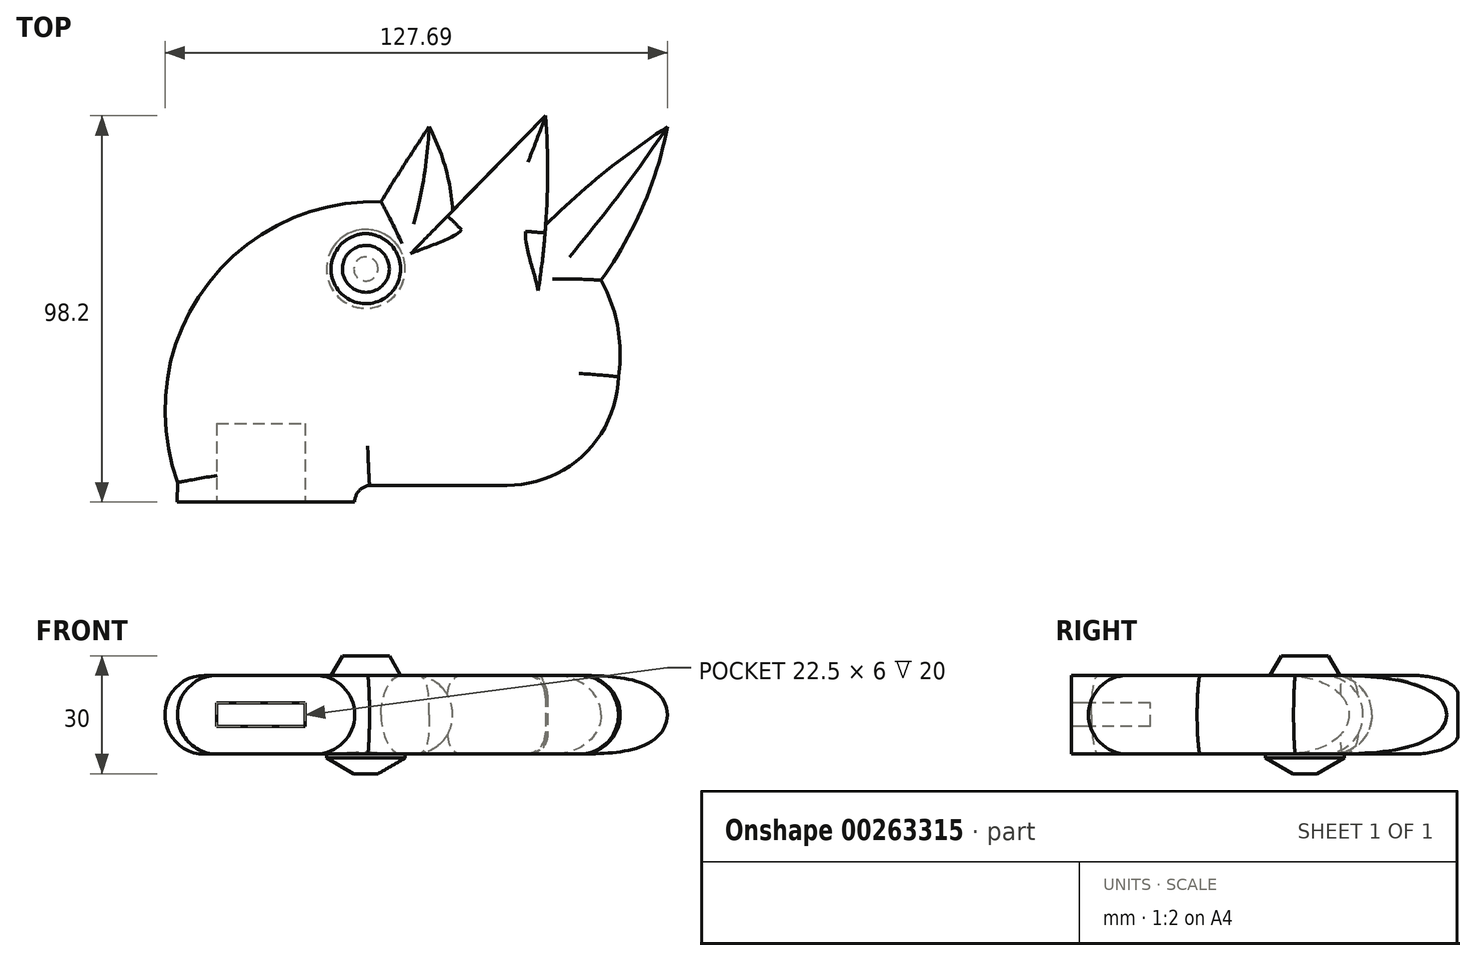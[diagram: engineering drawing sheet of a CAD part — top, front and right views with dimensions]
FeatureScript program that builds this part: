
annotation { "Feature Type Name" : "Feature", "Feature Type Description" : "" }
export const myFeature = defineFeature(function(context is Context, id is Id, definition is map)
    precondition{}
    {
        {
            var Q0;
            Q0=qCreatedBy(makeId("Top.planeOp"),FACE);
            var sketch = newSketch(context, id + "F0", { "sketchPlane" : qUnion([Q0])});
            skArc(sketch, "E0", {"start": v(-69.56, -48.3) * mm, "mid": v(-88.08, -45.25) * mm, "end": v(-106.8, -43.78) * mm});
            skArc(sketch, "E1", {"start": v(-106.8, -43.78) * mm, "mid": v(-96.39, -62.57) * mm, "end": v(-80.73, -77.27) * mm});
            skArc(sketch, "E2", {"start": v(-80.73, -77.27) * mm, "mid": v(-98.26, -84.7) * mm, "end": v(-114.23, -95.07) * mm});
            skArc(sketch, "E3", {"start": v(-114.23, -95.07) * mm, "mid": v(-98.6, -104.41) * mm, "end": v(-80.73, -107.98) * mm});
            skArc(sketch, "E4", {"start": v(-80.73, -107.98) * mm, "mid": v(-90.04, -123.58) * mm, "end": v(-94.69, -141.13) * mm});
            skArc(sketch, "E5", {"start": v(-94.69, -141.13) * mm, "mid": v(-78.8, -139.7) * mm, "end": v(-63.98, -133.8) * mm});
            skArc(sketch, "E6", {"start": v(-63.98, -133.8) * mm, "mid": v(40.14, -139.24) * mm, "end": v(30.94, -35.4) * mm});
            skArc(sketch, "E7", {"start": v(-31.41, -22.87) * mm, "mid": v(-53.17, -31.57) * mm, "end": v(-69.56, -48.3) * mm});
            skCircle(sketch, "E8", {"center": v(-12, -90) * mm, "radius": 35 * mm});
            skLineSegment(sketch, "E9", {"start": v(-12, -90) * mm, "end": v(-12, 0) * mm});
            skLineSegment(sketch, "E10", {"start": v(-12, 0) * mm, "end": v(0, 0) * mm});
            skLineSegment(sketch, "E11", {"start": v(-31.41, -22.87) * mm, "end": v(-12, 0) * mm});
            skLineSegment(sketch, "E12", {"start": v(-31.41, -22.87) * mm, "end": v(0, 0) * mm});
            skArc(sketch, "E13", {"start": v(30.94, -35.4) * mm, "mid": v(57.65, 8.29) * mm, "end": v(64.82, 58.99) * mm});
            skLineSegment(sketch, "E14", {"start": v(64.82, 42.9) * mm, "end": v(70.1, 125.75) * mm});
            skLineSegment(sketch, "E15", {"start": v(70.1, 125.75) * mm, "end": v(73.47, 146.99) * mm});
            skLineSegment(sketch, "E16", {"start": v(73.47, 146.99) * mm, "end": v(91.25, 150.97) * mm});
            skArc(sketch, "E17", {"start": v(93.55, 168.05) * mm, "mid": v(98.13, 170.3) * mm, "end": v(101.04, 174.5) * mm});
            skArc(sketch, "E18", {"start": v(101.04, 174.5) * mm, "mid": v(98.19, 178.86) * mm, "end": v(93.55, 181.22) * mm});
            skArc(sketch, "E19", {"start": v(91.25, 150.97) * mm, "mid": v(97.19, 153.5) * mm, "end": v(101.85, 157.96) * mm});
            skArc(sketch, "E20", {"start": v(101.85, 157.96) * mm, "mid": v(99.5, 164.5) * mm, "end": v(93.55, 168.05) * mm});
            skArc(sketch, "E21", {"start": v(93.55, 181.22) * mm, "mid": v(100.45, 185.24) * mm, "end": v(104.38, 192.2) * mm});
            skArc(sketch, "E22", {"start": v(16.27, 5.35) * mm, "mid": v(27.94, 20.47) * mm, "end": v(35.96, 37.8) * mm});
            skLineSegment(sketch, "E23", {"start": v(16.27, 5.35) * mm, "end": v(12.02, 0.97) * mm});
            skLineSegment(sketch, "E24", {"start": v(12.02, 54.47) * mm, "end": v(16.98, 220.58) * mm});
            skLineSegment(sketch, "E25", {"start": v(16.98, 220.58) * mm, "end": v(16.98, 230.48) * mm});
            skArc(sketch, "E26", {"start": v(20.74, 234.78) * mm, "mid": v(18.05, 233.34) * mm, "end": v(16.98, 230.48) * mm});
            skLineSegment(sketch, "E27", {"start": v(20.74, 234.78) * mm, "end": v(55.67, 234.78) * mm});
            skArc(sketch, "E28", {"start": v(55.67, 234.78) * mm, "mid": v(75.45, 242.82) * mm, "end": v(84, 262.38) * mm});
            skArc(sketch, "E29", {"start": v(84, 262.38) * mm, "mid": v(83.8, 275) * mm, "end": v(79.59, 286.9) * mm});
            skArc(sketch, "E30", {"start": v(79.59, 286.9) * mm, "mid": v(90.12, 305.47) * mm, "end": v(96.46, 325.87) * mm});
            skArc(sketch, "E31", {"start": v(96.46, 325.87) * mm, "mid": v(80.34, 314.22) * mm, "end": v(65.52, 300.95) * mm});
            skArc(sketch, "E32", {"start": v(65.52, 300.95) * mm, "mid": v(66.02, 314.82) * mm, "end": v(65.52, 328.68) * mm});
            skArc(sketch, "E33", {"start": v(41.86, 304.54) * mm, "mid": v(40.03, 315.53) * mm, "end": v(35.9, 325.87) * mm});
            skArc(sketch, "E34", {"start": v(35.9, 325.87) * mm, "mid": v(29.68, 316.4) * mm, "end": v(23.68, 306.81) * mm});
            skArc(sketch, "E35", {"start": v(23.68, 306.81) * mm, "mid": v(-21.12, 284.92) * mm, "end": v(-28, 235.53) * mm});
            skLineSegment(sketch, "E36", {"start": v(-31.41, -22.87) * mm, "end": v(-28, 235.53) * mm});
            skLineSegment(sketch, "E37", {"start": v(0, 0) * mm, "end": v(0, 302.13) * mm});
            skLineSegment(sketch, "E38", {"start": v(12.02, 0.97) * mm, "end": v(-31.41, -22.87) * mm});
            skLineSegment(sketch, "E39", {"start": v(0, 0) * mm, "end": v(12.02, 0.97) * mm});
            skLineSegment(sketch, "E40", {"start": v(12.02, 0.97) * mm, "end": v(30.94, -35.4) * mm});
            skLineSegment(sketch, "E41", {"start": v(64.82, 58.99) * mm, "end": v(46.6, 104.17) * mm});
            skLineSegment(sketch, "E42", {"start": v(12.02, 0.97) * mm, "end": v(12.02, 54.47) * mm});
            skLineSegment(sketch, "E43", {"start": v(-29.54, 119.27) * mm, "end": v(13.94, 118.7) * mm});
            skLineSegment(sketch, "E44", {"start": v(35.96, 37.8) * mm, "end": v(38.97, 138.47) * mm});
            skArc(sketch, "E45", {"start": v(104.38, 192.2) * mm, "mid": v(74.78, 206.52) * mm, "end": v(46.71, 189.39) * mm});
            skArc(sketch, "E46", {"start": v(46.71, 189.39) * mm, "mid": v(41.3, 164.16) * mm, "end": v(38.97, 138.47) * mm});
            skLineSegment(sketch, "E47", {"start": v(104.38, 192.2) * mm, "end": v(93.55, 181.22) * mm});
            skLineSegment(sketch, "E48", {"start": v(93.55, 168.05) * mm, "end": v(101.85, 157.96) * mm});
            skLineSegment(sketch, "E49", {"start": v(93.55, 181.22) * mm, "end": v(101.04, 174.5) * mm});
            skLineSegment(sketch, "E50", {"start": v(93.55, 168.05) * mm, "end": v(101.04, 174.5) * mm});
            skLineSegment(sketch, "E51", {"start": v(41.86, 304.54) * mm, "end": v(65.52, 328.68) * mm});
            skLineSegment(sketch, "E52", {"start": v(16.98, 230.48) * mm, "end": v(-28.07, 230.48) * mm});
            skLineSegment(sketch, "E53", {"start": v(12.02, 0.97) * mm, "end": v(-31.1, 0.49) * mm});
            skPoint(sketch, "E53.endSnap0", {"position": v(6.01, 0.49) * mm});
            skLineSegment(sketch, "E54", {"start": v(12.02, 0.97) * mm, "end": v(43.15, -20.17) * mm});
            skSolve(sketch);
        }
        {
            var Q0;
            {var subQ0=sQuery(id+"F0.wireOp",EDGE,"E38");var subQ1=sQuery(id+"F0.wireOp",EDGE,"E9");var subQ2=makeQuery(id+"F0.imprint","INTERSECT",VERTEX,{"derivedFrom":[subQ1,subQ0]});Q0=makeQuery(id+"F0.imprint","IMPRINT",FACE,{"disambiguationData":[TD([[makeQuery(id+"F0.imprint","IMPRINT",EDGE,{"disambiguationData":[TD([[subQ2,-1.0]])],"derivedFrom":subQ1}),1.0]])]});}
            var Q1;
            {var subQ0=sQuery(id+"F0.wireOp",EDGE,"E11");Q1=makeQuery(id+"F0.imprint","IMPRINT",FACE,{"disambiguationData":[TD([[makeQuery(id+"F0.imprint","IMPRINT",EDGE,{"derivedFrom":subQ0}),-1.0]])]});}
            var Q2;
            {var subQ0=sQuery(id+"F0.wireOp",EDGE,"E39");Q2=makeQuery(id+"F0.imprint","IMPRINT",FACE,{"disambiguationData":[TD([[makeQuery(id+"F0.imprint","IMPRINT",EDGE,{"derivedFrom":subQ0}),1.0]])]});}
            var Q3;
            Q3=makeQuery(id+"F0.imprint","IMPRINT",FACE,{"disambiguationData":[TD([[makeQuery(id+"F0.imprint","IMPRINT",EDGE,{"derivedFrom":sQuery(id+"F0.wireOp",EDGE,"E0")}),1.0]])]});
            var Q4;
            {var subQ5=sQuery(id+"F0.wireOp",EDGE,"E39");Q4=makeQuery(id+"F0.imprint","IMPRINT",FACE,{"disambiguationData":[TD([[makeQuery(id+"F0.imprint","IMPRINT",EDGE,{"derivedFrom":subQ5}),-1.0]])]});}
            var Q5;
            {var subQ2=sQuery(id+"F0.wireOp",EDGE,"E10");Q5=makeQuery(id+"F0.imprint","IMPRINT",FACE,{"disambiguationData":[TD([[makeQuery(id+"F0.imprint","IMPRINT",EDGE,{"derivedFrom":subQ2}),1.0]])]});}
            var Q6;
            {var subQ0=sQuery(id+"F0.wireOp",EDGE,"E10");Q6=makeQuery(id+"F0.imprint","IMPRINT",FACE,{"disambiguationData":[TD([[makeQuery(id+"F0.imprint","IMPRINT",EDGE,{"derivedFrom":subQ0}),-1.0]])]});}
            var Q7;
            {var subQ0=sQuery(id+"F0.wireOp",EDGE,"E40");Q7=makeQuery(id+"F0.imprint","IMPRINT",FACE,{"disambiguationData":[TD([[makeQuery(id+"F0.imprint","IMPRINT",EDGE,{"derivedFrom":subQ0}),1.0]])]});}
            extrude(context, id + "F1", {"entities" : qUnion([Q0, Q1, Q2, Q3, Q4, Q5, Q6, Q7]), "depth" : 20 * mm});
        }
        {
            var Q0;
            {var subQ1=sQuery(id+"F0.wireOp",EDGE,"E14");Q0=makeQuery(id+"F0.imprint","IMPRINT",FACE,{"disambiguationData":[TD([[makeQuery(id+"F0.imprint","IMPRINT",EDGE,{"derivedFrom":subQ1}),1.0]])]});}
            extrude(context, id + "F2", {"entities" : qUnion([Q0]), "depth" : 20 * mm});
        }
        {
            var Q0;
            {var subQ0=sQuery(id+"F0.wireOp",EDGE,"E43");var subQ1=sQuery(id+"F0.wireOp",EDGE,"E36");var subQ2=makeQuery(id+"F0.imprint","INTERSECT",VERTEX,{"derivedFrom":[subQ1,subQ0]});Q0=makeQuery(id+"F0.imprint","IMPRINT",FACE,{"disambiguationData":[TD([[makeQuery(id+"F0.imprint","IMPRINT",EDGE,{"disambiguationData":[TD([[subQ2,1.0]])],"derivedFrom":subQ1}),-1.0]])]});}
            var Q1;
            {var subQ5=sQuery(id+"F0.wireOp",EDGE,"E42");Q1=makeQuery(id+"F0.imprint","IMPRINT",FACE,{"disambiguationData":[TD([[makeQuery(id+"F0.imprint","IMPRINT",EDGE,{"derivedFrom":subQ5}),1.0]])]});}
            var Q2;
            {var subQ0=sQuery(id+"F0.wireOp",EDGE,"E43");var subQ1=sQuery(id+"F0.wireOp",EDGE,"E36");var subQ2=makeQuery(id+"F0.imprint","INTERSECT",VERTEX,{"derivedFrom":[subQ1,subQ0]});Q2=makeQuery(id+"F0.imprint","IMPRINT",FACE,{"disambiguationData":[TD([[makeQuery(id+"F0.imprint","IMPRINT",EDGE,{"disambiguationData":[TD([[subQ2,-1.0]])],"derivedFrom":subQ1}),-1.0]])]});}
            var Q3;
            {var subQ7=sQuery(id+"F0.wireOp",EDGE,"E25");Q3=makeQuery(id+"F0.imprint","IMPRINT",FACE,{"disambiguationData":[TD([[makeQuery(id+"F0.imprint","IMPRINT",EDGE,{"derivedFrom":subQ7}),1.0]])]});}
            extrude(context, id + "F3", {"entities" : qUnion([Q0, Q1, Q2, Q3]), "depth" : 20 * mm});
        }
        {
            var Q0;
            {var subQ0=sQuery(id+"F0.wireOp",EDGE,"E36");var subQ1=sQuery(id+"F0.wireOp",EDGE,"E35");var subQ2=makeQuery(id+"F0.imprint","INTERSECT",VERTEX,{"derivedFrom":[subQ1,subQ0]});Q0=makeQuery(id+"F0.imprint","IMPRINT",FACE,{"disambiguationData":[TD([[makeQuery(id+"F0.imprint","IMPRINT",EDGE,{"disambiguationData":[TD([[subQ2,1.0]])],"derivedFrom":subQ1}),1.0]])]});}
            var Q1;
            {var subQ4=sQuery(id+"F0.wireOp",EDGE,"E26");Q1=makeQuery(id+"F0.imprint","IMPRINT",FACE,{"disambiguationData":[TD([[makeQuery(id+"F0.imprint","IMPRINT",EDGE,{"derivedFrom":subQ4}),-1.0]])]});}
            extrude(context, id + "F4", {"entities" : qUnion([Q0, Q1]), "depth" : 20 * mm});
        }
        {
            var Q0;
            Q0=makeQuery(id+"F1.opExtrude","CAP_EDGE",EDGE,{"disambiguationData":[OSD([sQuery(id+"F0.wireOp",EDGE,"E36")])],"isStart":false});
            var Q1;
            Q1=makeQuery(id+"F1.opExtrude","CAP_EDGE",EDGE,{"disambiguationData":[OSD([sQuery(id+"F0.wireOp",EDGE,"E24")])],"isStart":false});
            var Q2;
            Q2=makeQuery(id+"F1.opExtrude","CAP_EDGE",EDGE,{"disambiguationData":[OSD([sQuery(id+"F0.wireOp",EDGE,"E42")])],"isStart":false});
            var Q3;
            Q3=makeQuery(id+"F1.opExtrude","CAP_EDGE",EDGE,{"disambiguationData":[OSD([sQuery(id+"F0.wireOp",EDGE,"E25")])],"isStart":false});
            var Q4;
            Q4=makeQuery(id+"F1.opExtrude","CAP_EDGE",EDGE,{"disambiguationData":[OSD([sQuery(id+"F0.wireOp",EDGE,"E35")])],"isStart":false});
            var Q5;
            Q5=makeQuery(id+"F1.opExtrude","CAP_EDGE",EDGE,{"disambiguationData":[OSD([sQuery(id+"F0.wireOp",EDGE,"E26")])],"isStart":false});
            var Q6;
            Q6=makeQuery(id+"F1.opExtrude","CAP_EDGE",EDGE,{"disambiguationData":[OSD([sQuery(id+"F0.wireOp",EDGE,"E42")])],"isStart":true});
            var Q7;
            Q7=makeQuery(id+"F1.opExtrude","CAP_EDGE",EDGE,{"disambiguationData":[OSD([sQuery(id+"F0.wireOp",EDGE,"E25")])],"isStart":true});
            var Q8;
            Q8=makeQuery(id+"F1.opExtrude","CAP_EDGE",EDGE,{"disambiguationData":[OSD([sQuery(id+"F0.wireOp",EDGE,"E36")])],"isStart":true});
            var Q9;
            Q9=makeQuery(id+"F1.opExtrude","CAP_EDGE",EDGE,{"disambiguationData":[OSD([sQuery(id+"F0.wireOp",EDGE,"E35")])],"isStart":true});
            var Q10;
            Q10=makeQuery(id+"F1.opExtrude","CAP_EDGE",EDGE,{"disambiguationData":[OSD([sQuery(id+"F0.wireOp",EDGE,"E26")])],"isStart":true});
            var Q11;
            Q11=makeQuery(id+"F1.opExtrude","CAP_EDGE",EDGE,{"disambiguationData":[OSD([sQuery(id+"F0.wireOp",EDGE,"E22")])],"isStart":false});
            var Q12;
            Q12=makeQuery(id+"F1.opExtrude","CAP_EDGE",EDGE,{"disambiguationData":[OSD([sQuery(id+"F0.wireOp",EDGE,"E23")])],"isStart":false});
            var Q13;
            Q13=makeQuery(id+"F1.opExtrude","CAP_EDGE",EDGE,{"disambiguationData":[OSD([sQuery(id+"F0.wireOp",EDGE,"E44")])],"isStart":false});
            var Q14;
            Q14=makeQuery(id+"F1.opExtrude","CAP_EDGE",EDGE,{"disambiguationData":[OSD([sQuery(id+"F0.wireOp",EDGE,"E45")])],"isStart":false});
            var Q15;
            Q15=makeQuery(id+"F1.opExtrude","CAP_EDGE",EDGE,{"disambiguationData":[OSD([sQuery(id+"F0.wireOp",EDGE,"E22")])],"isStart":true});
            var Q16;
            Q16=makeQuery(id+"F1.opExtrude","CAP_EDGE",EDGE,{"disambiguationData":[OSD([sQuery(id+"F0.wireOp",EDGE,"E44")])],"isStart":true});
            var Q17;
            Q17=makeQuery(id+"F1.opExtrude","CAP_EDGE",EDGE,{"disambiguationData":[OSD([sQuery(id+"F0.wireOp",EDGE,"E45")])],"isStart":true});
            var Q18;
            Q18=makeQuery(id+"F1.opExtrude","CAP_EDGE",EDGE,{"disambiguationData":[OSD([sQuery(id+"F0.wireOp",EDGE,"E13")])],"isStart":false});
            var Q19;
            Q19=makeQuery(id+"F1.opExtrude","CAP_EDGE",EDGE,{"disambiguationData":[OSD([sQuery(id+"F0.wireOp",EDGE,"E14")])],"isStart":false});
            var Q20;
            Q20=makeQuery(id+"F1.opExtrude","CAP_EDGE",EDGE,{"disambiguationData":[OSD([sQuery(id+"F0.wireOp",EDGE,"E15")])],"isStart":false});
            var Q21;
            Q21=makeQuery(id+"F1.opExtrude","CAP_EDGE",EDGE,{"disambiguationData":[OSD([sQuery(id+"F0.wireOp",EDGE,"E16")])],"isStart":false});
            var Q22;
            Q22=makeQuery(id+"F1.opExtrude","CAP_EDGE",EDGE,{"disambiguationData":[OSD([sQuery(id+"F0.wireOp",EDGE,"E16")])],"isStart":true});
            var Q23;
            Q23=makeQuery(id+"F1.opExtrude","CAP_EDGE",EDGE,{"disambiguationData":[OSD([sQuery(id+"F0.wireOp",EDGE,"E15")])],"isStart":true});
            var Q24;
            Q24=makeQuery(id+"F1.opExtrude","CAP_EDGE",EDGE,{"disambiguationData":[OSD([sQuery(id+"F0.wireOp",EDGE,"E14")])],"isStart":true});
            var Q25;
            Q25=makeQuery(id+"F1.opExtrude","CAP_EDGE",EDGE,{"disambiguationData":[OSD([sQuery(id+"F0.wireOp",EDGE,"E13")])],"isStart":true});
            var Q26;
            Q26=makeQuery(id+"F1.opExtrude","CAP_EDGE",EDGE,{"disambiguationData":[OSD([sQuery(id+"F0.wireOp",EDGE,"E6")])],"isStart":false});
            var Q27;
            Q27=makeQuery(id+"F1.opExtrude","CAP_EDGE",EDGE,{"disambiguationData":[OSD([sQuery(id+"F0.wireOp",EDGE,"E8")])],"isStart":false});
            var Q28;
            Q28=makeQuery(id+"F1.opExtrude","CAP_EDGE",EDGE,{"disambiguationData":[OSD([sQuery(id+"F0.wireOp",EDGE,"E7")])],"isStart":false});
            var Q29;
            Q29=makeQuery(id+"F1.opExtrude","CAP_EDGE",EDGE,{"disambiguationData":[OSD([sQuery(id+"F0.wireOp",EDGE,"E8")])],"isStart":true});
            var Q30;
            Q30=makeQuery(id+"F1.opExtrude","CAP_EDGE",EDGE,{"disambiguationData":[OSD([sQuery(id+"F0.wireOp",EDGE,"E7")])],"isStart":true});
            var Q31;
            Q31=makeQuery(id+"F1.opExtrude","CAP_EDGE",EDGE,{"disambiguationData":[OSD([sQuery(id+"F0.wireOp",EDGE,"E6")])],"isStart":true});
            fillet(context, id + "F5", {"entities" : qUnion([Q0, Q1, Q2, Q3, Q4, Q5, Q6, Q7, Q8, Q9, Q10, Q11, Q12, Q13, Q14, Q15, Q16, Q17, Q18, Q19, Q20, Q21, Q22, Q23, Q24, Q25, Q26, Q27, Q28, Q29, Q30, Q31]), "radius" : 10 * mm, "tangentPropagation" : true, "allowEdgeOverflow" : false});
        }
        {
            var Q0;
            Q0=makeQuery(id+"F1.opExtrude","CAP_EDGE",EDGE,{"disambiguationData":[OSD([sQuery(id+"F0.wireOp",EDGE,"E0")])],"isStart":false});
            var Q1;
            Q1=makeQuery(id+"F1.opExtrude","CAP_EDGE",EDGE,{"disambiguationData":[OSD([sQuery(id+"F0.wireOp",EDGE,"E1")])],"isStart":false});
            var Q2;
            Q2=makeQuery(id+"F1.opExtrude","CAP_EDGE",EDGE,{"disambiguationData":[OSD([sQuery(id+"F0.wireOp",EDGE,"E5")])],"isStart":false});
            var Q3;
            Q3=makeQuery(id+"F1.opExtrude","CAP_EDGE",EDGE,{"disambiguationData":[OSD([sQuery(id+"F0.wireOp",EDGE,"E4")])],"isStart":false});
            var Q4;
            Q4=makeQuery(id+"F1.opExtrude","CAP_EDGE",EDGE,{"disambiguationData":[OSD([sQuery(id+"F0.wireOp",EDGE,"E0")])],"isStart":true});
            var Q5;
            Q5=makeQuery(id+"F1.opExtrude","CAP_EDGE",EDGE,{"disambiguationData":[OSD([sQuery(id+"F0.wireOp",EDGE,"E1")])],"isStart":true});
            var Q6;
            Q6=makeQuery(id+"F1.opExtrude","CAP_EDGE",EDGE,{"disambiguationData":[OSD([sQuery(id+"F0.wireOp",EDGE,"E4")])],"isStart":true});
            var Q7;
            Q7=makeQuery(id+"F1.opExtrude","CAP_EDGE",EDGE,{"disambiguationData":[OSD([sQuery(id+"F0.wireOp",EDGE,"E5")])],"isStart":true});
            fillet(context, id + "F6", {"entities" : qUnion([Q0, Q1, Q2, Q3, Q4, Q5, Q6, Q7]), "radius" : 9.5 * mm, "tangentPropagation" : true, "rho" : 0.5, "crossSection" : FilletCrossSection.CONIC, "allowEdgeOverflow" : false});
        }
        {
            var Q0;
            Q0=makeQuery(id+"F1.opExtrude","CAP_EDGE",EDGE,{"disambiguationData":[OSD([sQuery(id+"F0.wireOp",EDGE,"E3")])],"isStart":true});
            var Q1;
            Q1=makeQuery(id+"F1.opExtrude","CAP_EDGE",EDGE,{"disambiguationData":[OSD([sQuery(id+"F0.wireOp",EDGE,"E2")])],"isStart":true});
            var Q2;
            Q2=makeQuery(id+"F1.opExtrude","CAP_EDGE",EDGE,{"disambiguationData":[OSD([sQuery(id+"F0.wireOp",EDGE,"E2")])],"isStart":false});
            var Q3;
            Q3=makeQuery(id+"F1.opExtrude","CAP_EDGE",EDGE,{"disambiguationData":[OSD([sQuery(id+"F0.wireOp",EDGE,"E3")])],"isStart":false});
            fillet(context, id + "F7", {"entities" : qUnion([Q0, Q1, Q2, Q3]), "radius" : 3 * mm, "tangentPropagation" : true, "allowEdgeOverflow" : false});
        }
        {
            var Q0;
            Q0=makeQuery(id+"F2.opExtrude","CAP_EDGE",EDGE,{"disambiguationData":[OSD([sQuery(id+"F0.wireOp",EDGE,"E14")])],"isStart":false});
            var Q1;
            Q1=makeQuery(id+"F2.opExtrude","CAP_EDGE",EDGE,{"disambiguationData":[OSD([sQuery(id+"F0.wireOp",EDGE,"E15")])],"isStart":false});
            var Q2;
            Q2=makeQuery(id+"F2.opExtrude","CAP_EDGE",EDGE,{"disambiguationData":[OSD([sQuery(id+"F0.wireOp",EDGE,"E14")])],"isStart":true});
            var Q3;
            Q3=makeQuery(id+"F2.opExtrude","CAP_EDGE",EDGE,{"disambiguationData":[OSD([sQuery(id+"F0.wireOp",EDGE,"E15")])],"isStart":true});
            var Q4;
            Q4=makeQuery(id+"F2.opExtrude","CAP_EDGE",EDGE,{"disambiguationData":[OSD([sQuery(id+"F0.wireOp",EDGE,"E16")])],"isStart":true});
            var Q5;
            Q5=makeQuery(id+"F2.opExtrude","CAP_EDGE",EDGE,{"disambiguationData":[OSD([sQuery(id+"F0.wireOp",EDGE,"E16")])],"isStart":false});
            var Q6;
            Q6=makeQuery(id+"F2.opExtrude","CAP_EDGE",EDGE,{"disambiguationData":[OSD([sQuery(id+"F0.wireOp",EDGE,"E45")])],"isStart":true});
            var Q7;
            Q7=makeQuery(id+"F2.opExtrude","CAP_EDGE",EDGE,{"disambiguationData":[OSD([sQuery(id+"F0.wireOp",EDGE,"E45")])],"isStart":false});
            var Q8;
            Q8=makeQuery(id+"F2.opExtrude","CAP_EDGE",EDGE,{"disambiguationData":[OSD([sQuery(id+"F0.wireOp",EDGE,"E46")])],"isStart":false});
            var Q9;
            Q9=makeQuery(id+"F2.opExtrude","CAP_EDGE",EDGE,{"disambiguationData":[OSD([sQuery(id+"F0.wireOp",EDGE,"E44")])],"isStart":false});
            var Q10;
            Q10=makeQuery(id+"F2.opExtrude","CAP_EDGE",EDGE,{"disambiguationData":[OSD([sQuery(id+"F0.wireOp",EDGE,"E22")])],"isStart":false});
            var Q11;
            Q11=makeQuery(id+"F2.opExtrude","CAP_EDGE",EDGE,{"disambiguationData":[OSD([sQuery(id+"F0.wireOp",EDGE,"E23")])],"isStart":false});
            var Q12;
            Q12=makeQuery(id+"F2.opExtrude","CAP_EDGE",EDGE,{"disambiguationData":[OSD([sQuery(id+"F0.wireOp",EDGE,"E46")])],"isStart":true});
            var Q13;
            Q13=makeQuery(id+"F2.opExtrude","CAP_EDGE",EDGE,{"disambiguationData":[OSD([sQuery(id+"F0.wireOp",EDGE,"E23")])],"isStart":true});
            var Q14;
            Q14=makeQuery(id+"F2.opExtrude","CAP_EDGE",EDGE,{"disambiguationData":[OSD([sQuery(id+"F0.wireOp",EDGE,"E22")])],"isStart":true});
            var Q15;
            Q15=makeQuery(id+"F2.opExtrude","CAP_EDGE",EDGE,{"disambiguationData":[OSD([sQuery(id+"F0.wireOp",EDGE,"E44")])],"isStart":true});
            var Q16;
            Q16=makeQuery(id+"F3.opExtrude","CAP_EDGE",EDGE,{"disambiguationData":[OSD([sQuery(id+"F0.wireOp",EDGE,"E24")])],"isStart":false});
            var Q17;
            Q17=makeQuery(id+"F3.opExtrude","CAP_EDGE",EDGE,{"disambiguationData":[OSD([sQuery(id+"F0.wireOp",EDGE,"E42")])],"isStart":false});
            var Q18;
            Q18=makeQuery(id+"F3.opExtrude","CAP_EDGE",EDGE,{"disambiguationData":[OSD([sQuery(id+"F0.wireOp",EDGE,"E42")])],"isStart":true});
            var Q19;
            Q19=makeQuery(id+"F3.opExtrude","CAP_EDGE",EDGE,{"disambiguationData":[OSD([sQuery(id+"F0.wireOp",EDGE,"E24")])],"isStart":true});
            var Q20;
            Q20=makeQuery(id+"F3.opExtrude","CAP_EDGE",EDGE,{"disambiguationData":[OSD([sQuery(id+"F0.wireOp",EDGE,"E25")])],"isStart":true});
            var Q21;
            Q21=makeQuery(id+"F3.opExtrude","CAP_EDGE",EDGE,{"disambiguationData":[OSD([sQuery(id+"F0.wireOp",EDGE,"E36")])],"isStart":false});
            var Q22;
            Q22=makeQuery(id+"F3.opExtrude","CAP_EDGE",EDGE,{"disambiguationData":[OSD([sQuery(id+"F0.wireOp",EDGE,"E36")])],"isStart":true});
            var Q23;
            Q23=makeQuery(id+"F4.opExtrude","CAP_EDGE",EDGE,{"disambiguationData":[OSD([sQuery(id+"F0.wireOp",EDGE,"E36")])],"isStart":true});
            var Q24;
            Q24=makeQuery(id+"F4.opExtrude","CAP_EDGE",EDGE,{"disambiguationData":[OSD([sQuery(id+"F0.wireOp",EDGE,"E36")])],"isStart":false});
            var Q25;
            Q25=makeQuery(id+"F4.opExtrude","CAP_EDGE",EDGE,{"disambiguationData":[OSD([sQuery(id+"F0.wireOp",EDGE,"E35")])],"isStart":true});
            var Q26;
            Q26=makeQuery(id+"F4.opExtrude","CAP_EDGE",EDGE,{"disambiguationData":[OSD([sQuery(id+"F0.wireOp",EDGE,"E35")])],"isStart":false});
            var Q27;
            Q27=makeQuery(id+"F4.opExtrude","CAP_EDGE",EDGE,{"disambiguationData":[OSD([sQuery(id+"F0.wireOp",EDGE,"E27")])],"isStart":false});
            var Q28;
            Q28=makeQuery(id+"F4.opExtrude","CAP_EDGE",EDGE,{"disambiguationData":[OSD([sQuery(id+"F0.wireOp",EDGE,"E28")])],"isStart":false});
            var Q29;
            Q29=makeQuery(id+"F4.opExtrude","CAP_EDGE",EDGE,{"disambiguationData":[OSD([sQuery(id+"F0.wireOp",EDGE,"E29")])],"isStart":false});
            var Q30;
            Q30=makeQuery(id+"F4.opExtrude","CAP_EDGE",EDGE,{"disambiguationData":[OSD([sQuery(id+"F0.wireOp",EDGE,"E27")])],"isStart":true});
            var Q31;
            Q31=makeQuery(id+"F4.opExtrude","CAP_EDGE",EDGE,{"disambiguationData":[OSD([sQuery(id+"F0.wireOp",EDGE,"E28")])],"isStart":true});
            var Q32;
            Q32=makeQuery(id+"F4.opExtrude","CAP_EDGE",EDGE,{"disambiguationData":[OSD([sQuery(id+"F0.wireOp",EDGE,"E29")])],"isStart":true});
            var Q33;
            Q33=makeQuery(id+"F4.opExtrude","CAP_EDGE",EDGE,{"disambiguationData":[OSD([sQuery(id+"F0.wireOp",EDGE,"E26")])],"isStart":false});
            var Q34;
            Q34=makeQuery(id+"F4.opExtrude","CAP_EDGE",EDGE,{"disambiguationData":[OSD([sQuery(id+"F0.wireOp",EDGE,"E26")])],"isStart":true});
            var Q35;
            Q35=makeQuery(id+"F4.opExtrude","CAP_EDGE",EDGE,{"disambiguationData":[OSD([sQuery(id+"F0.wireOp",EDGE,"E30")])],"isStart":false});
            var Q36;
            Q36=makeQuery(id+"F4.opExtrude","CAP_EDGE",EDGE,{"disambiguationData":[OSD([sQuery(id+"F0.wireOp",EDGE,"E31")])],"isStart":false});
            var Q37;
            Q37=makeQuery(id+"F4.opExtrude","CAP_EDGE",EDGE,{"disambiguationData":[OSD([sQuery(id+"F0.wireOp",EDGE,"E30")])],"isStart":true});
            var Q38;
            Q38=makeQuery(id+"F4.opExtrude","CAP_EDGE",EDGE,{"disambiguationData":[OSD([sQuery(id+"F0.wireOp",EDGE,"E31")])],"isStart":true});
            var Q39;
            Q39=makeQuery(id+"F4.opExtrude","CAP_EDGE",EDGE,{"disambiguationData":[OSD([sQuery(id+"F0.wireOp",EDGE,"E33")])],"isStart":false});
            var Q40;
            Q40=makeQuery(id+"F4.opExtrude","CAP_EDGE",EDGE,{"disambiguationData":[OSD([sQuery(id+"F0.wireOp",EDGE,"E34")])],"isStart":false});
            var Q41;
            Q41=makeQuery(id+"F4.opExtrude","CAP_EDGE",EDGE,{"disambiguationData":[OSD([sQuery(id+"F0.wireOp",EDGE,"E34")])],"isStart":true});
            var Q42;
            Q42=makeQuery(id+"F4.opExtrude","CAP_EDGE",EDGE,{"disambiguationData":[OSD([sQuery(id+"F0.wireOp",EDGE,"E33")])],"isStart":true});
            fillet(context, id + "F8", {"entities" : qUnion([Q0, Q1, Q2, Q3, Q4, Q5, Q6, Q7, Q8, Q9, Q10, Q11, Q12, Q13, Q14, Q15, Q16, Q17, Q18, Q19, Q20, Q21, Q22, Q23, Q24, Q25, Q26, Q27, Q28, Q29, Q30, Q31, Q32, Q33, Q34, Q35, Q36, Q37, Q38, Q39, Q40, Q41, Q42]), "radius" : 10 * mm, "tangentPropagation" : true, "allowEdgeOverflow" : false});
        }
        {
            var Q0;
            Q0=makeQuery(id+"F4.opExtrude","CAP_EDGE",EDGE,{"disambiguationData":[OSD([sQuery(id+"F0.wireOp",EDGE,"E51")])],"isStart":false});
            var Q1;
            Q1=makeQuery(id+"F4.opExtrude","CAP_EDGE",EDGE,{"disambiguationData":[OSD([sQuery(id+"F0.wireOp",EDGE,"E32")])],"isStart":false});
            var Q2;
            Q2=makeQuery(id+"F4.opExtrude","CAP_EDGE",EDGE,{"disambiguationData":[OSD([sQuery(id+"F0.wireOp",EDGE,"E32")])],"isStart":true});
            var Q3;
            Q3=makeQuery(id+"F4.opExtrude","CAP_EDGE",EDGE,{"disambiguationData":[OSD([sQuery(id+"F0.wireOp",EDGE,"E51")])],"isStart":true});
            fillet(context, id + "F9", {"entities" : qUnion([Q0, Q1, Q2, Q3]), "radius" : 5 * mm, "tangentPropagation" : true, "allowEdgeOverflow" : false});
        }
        {
            var Q0;
            Q0=makeQuery(id+"F2.opExtrude","CAP_EDGE",EDGE,{"disambiguationData":[OSD([sQuery(id+"F0.wireOp",EDGE,"E50")])],"isStart":true});
            var Q1;
            Q1=makeQuery(id+"F2.opExtrude","CAP_EDGE",EDGE,{"disambiguationData":[OSD([sQuery(id+"F0.wireOp",EDGE,"E49")])],"isStart":true});
            var Q2;
            Q2=makeQuery(id+"F2.opExtrude","CAP_EDGE",EDGE,{"disambiguationData":[OSD([sQuery(id+"F0.wireOp",EDGE,"E49")])],"isStart":false});
            var Q3;
            Q3=makeQuery(id+"F2.opExtrude","CAP_EDGE",EDGE,{"disambiguationData":[OSD([sQuery(id+"F0.wireOp",EDGE,"E50")])],"isStart":false});
            var Q4;
            Q4=makeQuery(id+"F8.opFillet","BLEND_EDGE",EDGE,{"blendedFrom":[makeQuery(id+"F2.opExtrude","CAP_EDGE",EDGE,{"disambiguationData":[OSD([sQuery(id+"F0.wireOp",EDGE,"E45")])],"isStart":false}),makeQuery(id+"F2.opExtrude","SWEPT_FACE",FACE,{"disambiguationData":[OSD([sQuery(id+"F0.wireOp",EDGE,"E47")])]})],"blendedInto":[makeQuery(id+"F2.opExtrude","SWEPT_FACE",FACE,{"disambiguationData":[OSD([sQuery(id+"F0.wireOp",EDGE,"E47")])]})]});
            var Q5;
            Q5=makeQuery(id+"F8.opFillet","BLEND_EDGE",EDGE,{"blendedFrom":[makeQuery(id+"F2.opExtrude","CAP_EDGE",EDGE,{"disambiguationData":[OSD([sQuery(id+"F0.wireOp",EDGE,"E19")])],"isStart":false}),makeQuery(id+"F2.opExtrude","SWEPT_FACE",FACE,{"disambiguationData":[OSD([sQuery(id+"F0.wireOp",EDGE,"E48")])]})],"blendedInto":[makeQuery(id+"F2.opExtrude","SWEPT_FACE",FACE,{"disambiguationData":[OSD([sQuery(id+"F0.wireOp",EDGE,"E48")])]})]});
            fillet(context, id + "F10", {"entities" : qUnion([Q0, Q1, Q2, Q3, Q4, Q5]), "radius" : 5 * mm, "tangentPropagation" : true, "allowEdgeOverflow" : false});
        }
        {
            var Q0;
            Q0=makeQuery(id+"F5.opFillet","SPLIT",FACE,{"disambiguationData":[OD(0.0)],"derivedFrom":makeQuery(id+"F1.opExtrude","CAP_FACE",FACE,{"disambiguationData":[OSD([sQuery(id+"F0.wireOp",EDGE,"E0"),sQuery(id+"F0.wireOp",EDGE,"E1"),sQuery(id+"F0.wireOp",EDGE,"E2"),sQuery(id+"F0.wireOp",EDGE,"E3"),sQuery(id+"F0.wireOp",EDGE,"E4"),sQuery(id+"F0.wireOp",EDGE,"E5"),sQuery(id+"F0.wireOp",EDGE,"E6"),sQuery(id+"F0.wireOp",EDGE,"E7"),sQuery(id+"F0.wireOp",EDGE,"E8"),sQuery(id+"F0.wireOp",EDGE,"E13"),sQuery(id+"F0.wireOp",EDGE,"E14"),sQuery(id+"F0.wireOp",EDGE,"E15"),sQuery(id+"F0.wireOp",EDGE,"E16"),sQuery(id+"F0.wireOp",EDGE,"E19"),sQuery(id+"F0.wireOp",EDGE,"E22"),sQuery(id+"F0.wireOp",EDGE,"E23"),sQuery(id+"F0.wireOp",EDGE,"E24"),sQuery(id+"F0.wireOp",EDGE,"E25"),sQuery(id+"F0.wireOp",EDGE,"E26"),sQuery(id+"F0.wireOp",EDGE,"E27"),sQuery(id+"F0.wireOp",EDGE,"E28"),sQuery(id+"F0.wireOp",EDGE,"E29"),sQuery(id+"F0.wireOp",EDGE,"E30"),sQuery(id+"F0.wireOp",EDGE,"E31"),sQuery(id+"F0.wireOp",EDGE,"E32"),sQuery(id+"F0.wireOp",EDGE,"E33"),sQuery(id+"F0.wireOp",EDGE,"E34"),sQuery(id+"F0.wireOp",EDGE,"E35"),sQuery(id+"F0.wireOp",EDGE,"E36"),sQuery(id+"F0.wireOp",EDGE,"E42"),sQuery(id+"F0.wireOp",EDGE,"E44"),sQuery(id+"F0.wireOp",EDGE,"E45"),sQuery(id+"F0.wireOp",EDGE,"E46"),sQuery(id+"F0.wireOp",EDGE,"E47"),sQuery(id+"F0.wireOp",EDGE,"E48"),sQuery(id+"F0.wireOp",EDGE,"E49"),sQuery(id+"F0.wireOp",EDGE,"E50"),sQuery(id+"F0.wireOp",EDGE,"E51")])],"isStart":false})});
            var sketch = newSketch(context, id + "F11", { "sketchPlane" : qUnion([Q0])});
            skLineSegment(sketch, "E55", {"start": v(0, 0) * mm, "end": v(3.83, 289.97) * mm});
            skLineSegment(sketch, "E56", {"start": v(3.83, 289.97) * mm, "end": v(19.83, 289.76) * mm});
            skCircle(sketch, "E57", {"center": v(19.83, 289.76) * mm, "radius": 10 * mm});
            skSolve(sketch);
        }
        {
            var Q0;
            Q0=makeQuery(id+"F11.imprint","IMPRINT",FACE,{"disambiguationData":[TD([[makeQuery(id+"F11.imprint","IMPRINT",EDGE,{"derivedFrom":sQuery(id+"F11.wireOp",EDGE,"E57")}),1.0]])]});
            extrude(context, id + "F12", {"entities" : qUnion([Q0]), "operationType" : NewBodyOperationType.ADD, "depth" : 5 * mm, "hasSecondDirection" : true, "secondDirectionOppositeDirection" : true, "secondDirectionDepth" : 25 * mm});
        }
        {
            var Q0;
            Q0=makeQuery(id+"F12.opExtrude","CAP_EDGE",EDGE,{"disambiguationData":[OSD([sQuery(id+"F11.wireOp",EDGE,"E57")])],"isStart":false});
            chamfer(context, id + "F13", {"entities" : qUnion([Q0]), "chamferType" : ChamferType.OFFSET_ANGLE, "width" : 7 * mm, "oppositeDirection" : false, "angle" : 30 * degree, "tangentPropagation" : true});
        }
        {
            var Q0;
            Q0=makeQuery(id+"F12.opExtrude","CAP_EDGE",EDGE,{"disambiguationData":[OSD([sQuery(id+"F11.wireOp",EDGE,"E57")])],"isStart":true});
            chamfer(context, id + "F14", {"entities" : qUnion([Q0]), "chamferType" : ChamferType.OFFSET_ANGLE, "width" : 4 * mm, "oppositeDirection" : false, "angle" : 60 * degree, "tangentPropagation" : true});
        }
        {
            var Q0;
            Q0=makeQuery(id+"F1.opExtrude","SWEPT_BODY",BODY,{"disambiguationData":[OSD([sQuery(id+"F0.wireOp",EDGE,"E0"),sQuery(id+"F0.wireOp",EDGE,"E1"),sQuery(id+"F0.wireOp",EDGE,"E2"),sQuery(id+"F0.wireOp",EDGE,"E3"),sQuery(id+"F0.wireOp",EDGE,"E4"),sQuery(id+"F0.wireOp",EDGE,"E5"),sQuery(id+"F0.wireOp",EDGE,"E6"),sQuery(id+"F0.wireOp",EDGE,"E7"),sQuery(id+"F0.wireOp",EDGE,"E8"),sQuery(id+"F0.wireOp",EDGE,"E13"),sQuery(id+"F0.wireOp",EDGE,"E36"),sQuery(id+"F0.wireOp",EDGE,"E53"),sQuery(id+"F0.wireOp",EDGE,"E54")])]});
            var Q1;
            Q1=makeQuery(id+"F3.opExtrude","SWEPT_BODY",BODY,{"disambiguationData":[OSD([sQuery(id+"F0.wireOp",EDGE,"E24"),sQuery(id+"F0.wireOp",EDGE,"E25"),sQuery(id+"F0.wireOp",EDGE,"E36"),sQuery(id+"F0.wireOp",EDGE,"E42"),sQuery(id+"F0.wireOp",EDGE,"E52"),sQuery(id+"F0.wireOp",EDGE,"E53")])]});
            var Q2;
            Q2=makeQuery(id+"F2.opExtrude","SWEPT_BODY",BODY,{"disambiguationData":[OSD([sQuery(id+"F0.wireOp",EDGE,"E13"),sQuery(id+"F0.wireOp",EDGE,"E14"),sQuery(id+"F0.wireOp",EDGE,"E15"),sQuery(id+"F0.wireOp",EDGE,"E16"),sQuery(id+"F0.wireOp",EDGE,"E19"),sQuery(id+"F0.wireOp",EDGE,"E22"),sQuery(id+"F0.wireOp",EDGE,"E23"),sQuery(id+"F0.wireOp",EDGE,"E44"),sQuery(id+"F0.wireOp",EDGE,"E45"),sQuery(id+"F0.wireOp",EDGE,"E46"),sQuery(id+"F0.wireOp",EDGE,"E47"),sQuery(id+"F0.wireOp",EDGE,"E48"),sQuery(id+"F0.wireOp",EDGE,"E49"),sQuery(id+"F0.wireOp",EDGE,"E50"),sQuery(id+"F0.wireOp",EDGE,"E54")])]});
            deleteBodies(context, id + "F15", {"entities" : qUnion([Q0, Q1, Q2])});
        }
        {
            var Q0;
            Q0=makeQuery(id+"F4.opExtrude","SWEPT_FACE",FACE,{"disambiguationData":[OSD([sQuery(id+"F0.wireOp",EDGE,"E52")])]});
            var sketch = newSketch(context, id + "F16", { "sketchPlane" : qUnion([Q0])});
            skLineSegment(sketch, "E58", {"start": v(-28.07, 10) * mm, "end": v(-18.07, 10) * mm});
            skLineSegment(sketch, "E59", {"start": v(-18.07, 10) * mm, "end": v(-18.07, 13) * mm});
            skLineSegment(sketch, "E60.bottom", {"start": v(-18.07, 13) * mm, "end": v(4.43, 13) * mm});
            skLineSegment(sketch, "E60.top", {"start": v(-18.07, 7) * mm, "end": v(4.43, 7) * mm});
            skLineSegment(sketch, "E60.left", {"start": v(-18.07, 13) * mm, "end": v(-18.07, 7) * mm});
            skLineSegment(sketch, "E60.right", {"start": v(4.43, 13) * mm, "end": v(4.43, 7) * mm});
            skSolve(sketch);
        }
        {
            var Q0;
            Q0 = qSketchRegion(id + "F16", true);
            extrude(context, id + "F17", {"entities" : qUnion([Q0]), "operationType" : NewBodyOperationType.REMOVE, "oppositeDirection" : true, "depth" : 20 * mm});
        }
    });
